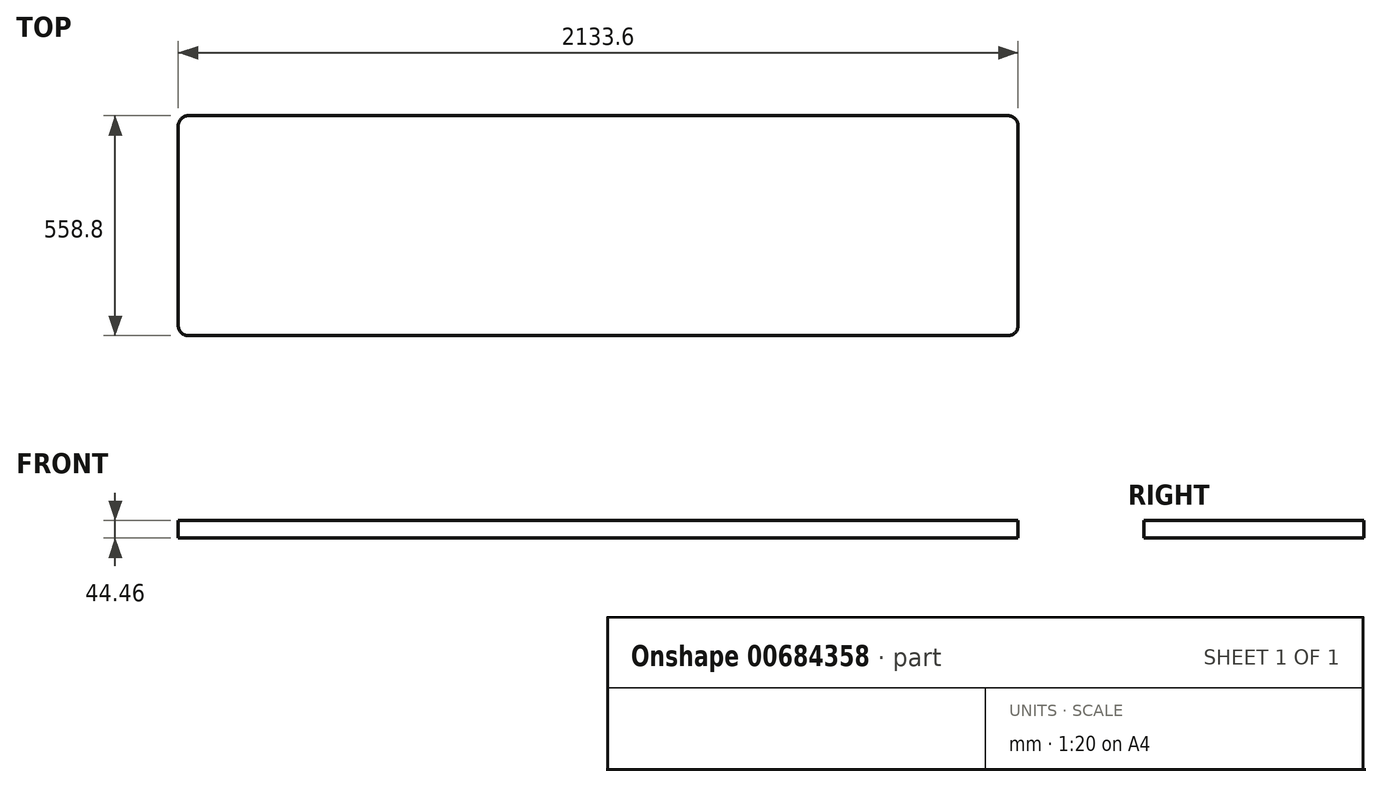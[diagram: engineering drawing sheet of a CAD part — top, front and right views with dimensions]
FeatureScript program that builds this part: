
annotation { "Feature Type Name" : "Feature", "Feature Type Description" : "" }
export const myFeature = defineFeature(function(context is Context, id is Id, definition is map)
    precondition{}
    {
        {
            var Q0;
            Q0=qCreatedBy(makeId("Top.planeOp"),FACE);
            var sketch = newSketch(context, id + "F0", { "sketchPlane" : qUnion([Q0])});
            skLineSegment(sketch, "E0.bottom", {"start": v(1066.8, 279.4) * mm, "end": v(-1066.8, 279.4) * mm});
            skLineSegment(sketch, "E0.top", {"start": v(1066.8, -279.4) * mm, "end": v(-1066.8, -279.4) * mm});
            skLineSegment(sketch, "E0.left", {"start": v(1066.8, 279.4) * mm, "end": v(1066.8, -279.4) * mm});
            skLineSegment(sketch, "E0.right", {"start": v(-1066.8, 279.4) * mm, "end": v(-1066.8, -279.4) * mm});
            skPoint(sketch, "E0.middle", {"position": v(0, 0) * mm});
            skSolve(sketch);
        }
        {
            var Q0;
            Q0 = qSketchRegion(id + "F0", true);
            extrude(context, id + "F1", {"entities" : qUnion([Q0]), "endBound" : BoundingType.SYMMETRIC, "depth" : 44.45 * mm, "offsetDistance" : 25.4 * mm});
        }
        {
            var Q0;
            Q0=makeQuery(id+"F1.opExtrude","SWEPT_EDGE",EDGE,{"disambiguationData":[OSD([sQuery(id+"F0.wireOp",EDGE,"E0.top"),sQuery(id+"F0.wireOp",EDGE,"E0.left")])]});
            var Q1;
            Q1=makeQuery(id+"F1.opExtrude","SWEPT_EDGE",EDGE,{"disambiguationData":[OSD([sQuery(id+"F0.wireOp",EDGE,"E0.bottom"),sQuery(id+"F0.wireOp",EDGE,"E0.left")])]});
            var Q2;
            Q2=makeQuery(id+"F1.opExtrude","SWEPT_EDGE",EDGE,{"disambiguationData":[OSD([sQuery(id+"F0.wireOp",EDGE,"E0.top"),sQuery(id+"F0.wireOp",EDGE,"E0.right")])]});
            var Q3;
            Q3=makeQuery(id+"F1.opExtrude","SWEPT_EDGE",EDGE,{"disambiguationData":[OSD([sQuery(id+"F0.wireOp",EDGE,"E0.bottom"),sQuery(id+"F0.wireOp",EDGE,"E0.right")])]});
            fillet(context, id + "F2", {"entities" : qUnion([Q0, Q1, Q2, Q3]), "radius" : 25.4 * mm, "tangentPropagation" : true, "allowEdgeOverflow" : false});
        }
    });
